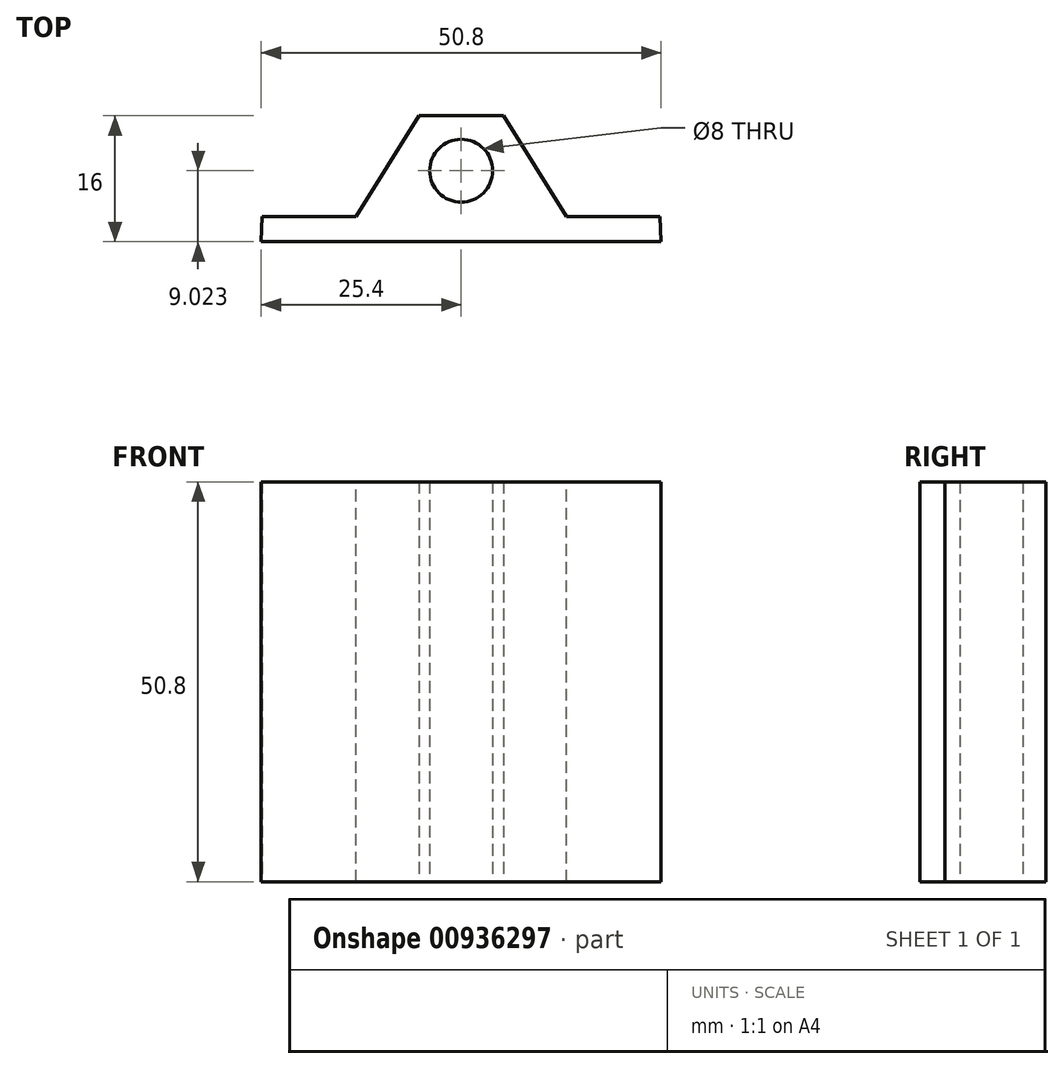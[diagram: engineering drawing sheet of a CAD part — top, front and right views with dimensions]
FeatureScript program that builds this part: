
annotation { "Feature Type Name" : "Feature", "Feature Type Description" : "" }
export const myFeature = defineFeature(function(context is Context, id is Id, definition is map)
    precondition{}
    {
        {
            var Q0;
            Q0=qCreatedBy(makeId("Top.planeOp"),FACE);
            var sketch = newSketch(context, id + "F0", { "sketchPlane" : qUnion([Q0])});
            skLineSegment(sketch, "E0", {"start": v(0, 0) * mm, "end": v(25.4, 0) * mm});
            skLineSegment(sketch, "E1", {"start": v(0, 3.18) * mm, "end": v(25.27, 3.18) * mm});
            skLineSegment(sketch, "E2", {"start": v(25.27, 3.17) * mm, "end": v(25.4, 0) * mm});
            skLineSegment(sketch, "E3.MirrorCS", {"start": v(0, 3.18) * mm, "end": v(-25.27, 3.18) * mm});
            skLineSegment(sketch, "E4.MirrorCS", {"start": v(0, 0) * mm, "end": v(-25.4, 0) * mm});
            skLineSegment(sketch, "E5.MirrorCS", {"start": v(-25.27, 3.18) * mm, "end": v(-25.4, 0) * mm});
            skSolve(sketch);
        }
        {
            var Q0;
            Q0=makeQuery(id+"F0.imprint","IMPRINT",FACE,{"disambiguationData":[TD([[makeQuery(id+"F0.imprint","IMPRINT",EDGE,{"derivedFrom":sQuery(id+"F0.wireOp",EDGE,"E0")}),1.0]])]});
            extrude(context, id + "F1", {"entities" : qUnion([Q0]), "endBound" : BoundingType.SYMMETRIC, "depth" : 50.8 * mm, "offsetDistance" : 25.4 * mm});
        }
        {
            var Q0;
            Q0=qCreatedBy(makeId("Top.planeOp"),FACE);
            var sketch = newSketch(context, id + "F2", { "sketchPlane" : qUnion([Q0])});
            skPoint(sketch, "E6", {"position": v(0, 16) * mm});
            skLineSegment(sketch, "E7", {"start": v(-15.35, 0) * mm, "end": v(15.35, 0) * mm});
            skCircle(sketch, "E8", {"center": v(0, 9.02) * mm, "radius": 4 * mm});
            skLineSegment(sketch, "E9", {"start": v(0, 16) * mm, "end": v(5.35, 16) * mm});
            skLineSegment(sketch, "E10", {"start": v(15.35, 0) * mm, "end": v(5.35, 16) * mm});
            skLineSegment(sketch, "E11.MirrorCS", {"start": v(0, 16) * mm, "end": v(-5.35, 16) * mm});
            skLineSegment(sketch, "E12.MirrorCS", {"start": v(-15.35, 0) * mm, "end": v(-5.35, 16) * mm});
            skSolve(sketch);
        }
        {
            var Q0;
            Q0=makeQuery(id+"F2.imprint","IMPRINT",FACE,{"disambiguationData":[TD([[makeQuery(id+"F2.imprint","IMPRINT",EDGE,{"derivedFrom":sQuery(id+"F2.wireOp",EDGE,"E7")}),1.0]])]});
            extrude(context, id + "F3", {"entities" : qUnion([Q0]), "operationType" : NewBodyOperationType.ADD, "endBound" : BoundingType.SYMMETRIC, "depth" : 50.8 * mm, "offsetDistance" : 25.4 * mm});
        }
    });
